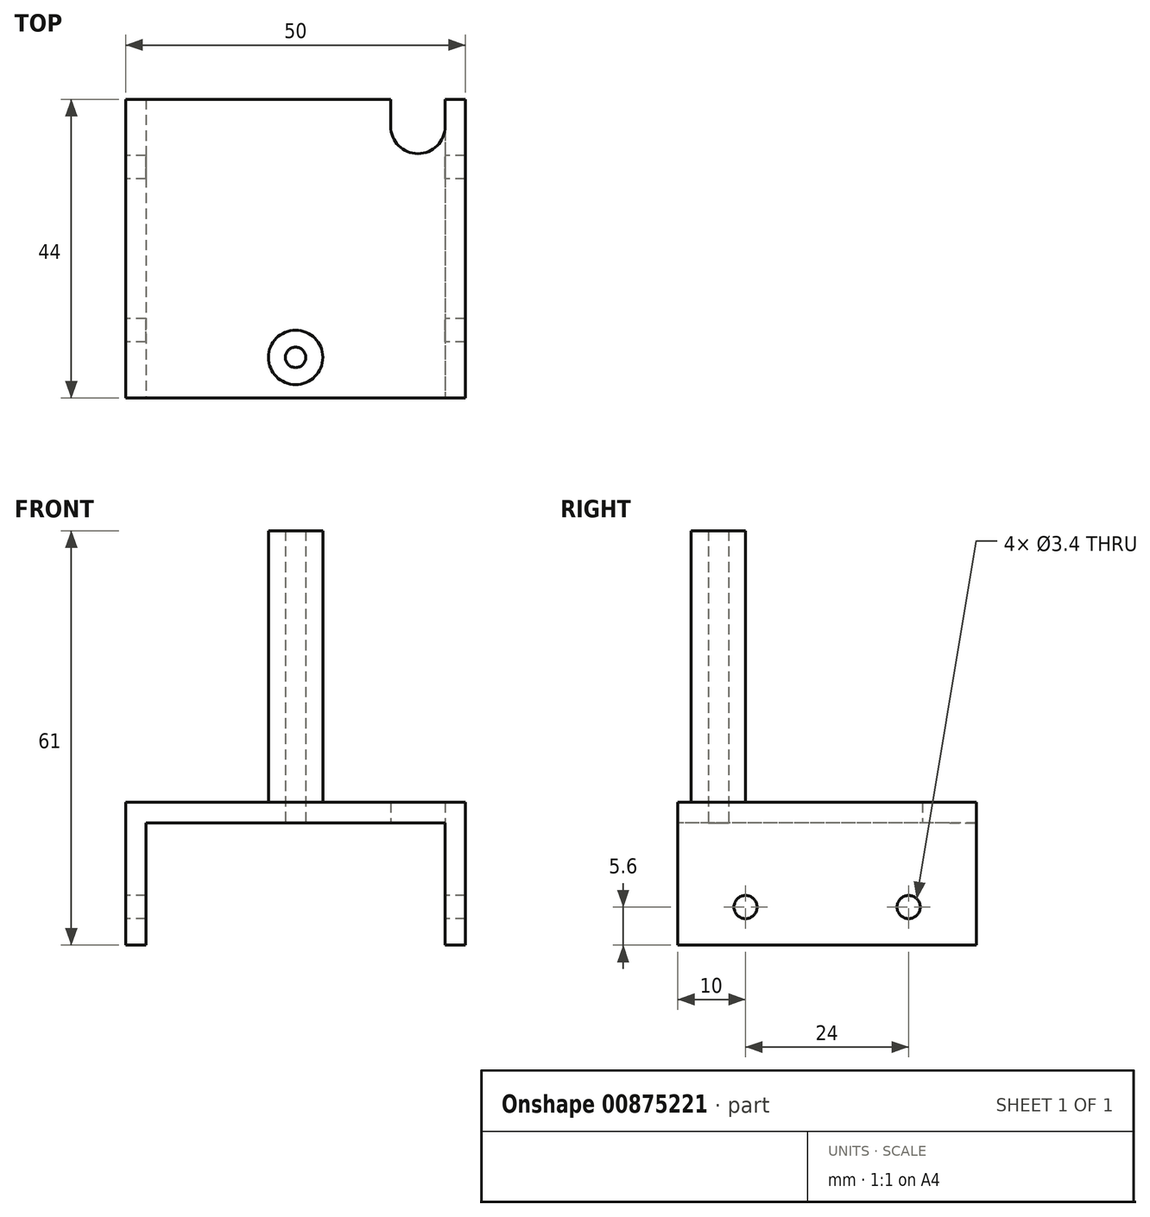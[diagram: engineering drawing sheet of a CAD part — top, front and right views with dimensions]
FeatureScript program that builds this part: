
annotation { "Feature Type Name" : "Feature", "Feature Type Description" : "" }
export const myFeature = defineFeature(function(context is Context, id is Id, definition is map)
    precondition{}
    {
        {
            var Q0;
            Q0=qCreatedBy(makeId("Top.planeOp"),FACE);
            var sketch = newSketch(context, id + "F0", { "sketchPlane" : qUnion([Q0])});
            skLineSegment(sketch, "E0.bottom", {"start": v(-22, 22) * mm, "end": v(22, 22) * mm});
            skLineSegment(sketch, "E0.top", {"start": v(-22, -22) * mm, "end": v(22, -22) * mm});
            skLineSegment(sketch, "E0.left", {"start": v(-22, 22) * mm, "end": v(-22, -22) * mm});
            skLineSegment(sketch, "E0.right", {"start": v(22, 22) * mm, "end": v(22, -22) * mm});
            skPoint(sketch, "E0.middle", {"position": v(0, 0) * mm});
            skCircle(sketch, "E1", {"center": v(18, 18) * mm, "radius": 4 * mm});
            skLineSegment(sketch, "E2", {"start": v(18, 18) * mm, "end": v(18, 22) * mm});
            skLineSegment(sketch, "E3", {"start": v(18, 18) * mm, "end": v(22, 18) * mm});
            skCircle(sketch, "E4", {"center": v(-17, -10) * mm, "radius": 1.7 * mm, "construction": true});
            skCircle(sketch, "E5", {"center": v(0, -16) * mm, "radius": 1.5 * mm});
            skCircle(sketch, "E6", {"center": v(3, -10) * mm, "radius": 1.7 * mm, "construction": true});
            skLineSegment(sketch, "E7", {"start": v(-22, -10) * mm, "end": v(22, -10) * mm, "construction": true});
            skLineSegment(sketch, "E8.bottom", {"start": v(-25, 22) * mm, "end": v(25, 22) * mm});
            skLineSegment(sketch, "E8.top", {"start": v(-25, -22) * mm, "end": v(25, -22) * mm});
            skLineSegment(sketch, "E8.left", {"start": v(-25, 22) * mm, "end": v(-25, -22) * mm});
            skLineSegment(sketch, "E8.right", {"start": v(25, 22) * mm, "end": v(25, -22) * mm});
            skCircle(sketch, "E9", {"center": v(0, -16) * mm, "radius": 4 * mm});
            skLineSegment(sketch, "E10", {"start": v(22, 18) * mm, "end": v(14, 18) * mm, "construction": true});
            skLineSegment(sketch, "E11", {"start": v(14, 18) * mm, "end": v(14, 22) * mm});
            skLineSegment(sketch, "E12.left", {"start": v(14, 22) * mm, "end": v(14, 18.38) * mm});
            skLineSegment(sketch, "E13.bottom", {"start": v(-22, 22) * mm, "end": v(22, 22) * mm, "construction": true});
            skLineSegment(sketch, "E14.top", {"start": v(-22, -14) * mm, "end": v(22, -14) * mm, "construction": true});
            skLineSegment(sketch, "E14.left", {"start": v(-22, -10) * mm, "end": v(-22, -14) * mm, "construction": true});
            skLineSegment(sketch, "E14.right", {"start": v(22, -10) * mm, "end": v(22, -14) * mm, "construction": true});
            skSolve(sketch);
        }
        {
            var Q0;
            {var subQ1=sQuery(id+"F0.wireOp",EDGE,"E0.top");Q0=makeQuery(id+"F0.imprint","IMPRINT",FACE,{"disambiguationData":[TD([[makeQuery(id+"F0.imprint","IMPRINT",EDGE,{"derivedFrom":subQ1}),1.0]])]});}
            var Q1;
            {var subQ0=sQuery(id+"F0.wireOp",EDGE,"E0.left");Q1=makeQuery(id+"F0.imprint","IMPRINT",FACE,{"disambiguationData":[TD([[makeQuery(id+"F0.imprint","IMPRINT",EDGE,{"derivedFrom":subQ0}),-1.0]])]});}
            var Q2;
            {var subQ1=sQuery(id+"F0.wireOp",EDGE,"E0.top");Q2=makeQuery(id+"F0.imprint","IMPRINT",FACE,{"disambiguationData":[TD([[makeQuery(id+"F0.imprint","IMPRINT",EDGE,{"derivedFrom":subQ1}),1.0]])]});}
            var Q3;
            {var subQ3=sQuery(id+"F0.wireOp",EDGE,"E8.right");Q3=makeQuery(id+"F0.imprint","IMPRINT",FACE,{"disambiguationData":[TD([[makeQuery(id+"F0.imprint","IMPRINT",EDGE,{"derivedFrom":subQ3}),-1.0]])]});}
            var Q4;
            Q4=makeQuery(id+"F0.imprint","IMPRINT",FACE,{"disambiguationData":[TD([[makeQuery(id+"F0.imprint","IMPRINT",EDGE,{"derivedFrom":sQuery(id+"F0.wireOp",EDGE,"E5")}),-1.0]])]});
            var Q5;
            Q5=makeQuery(id+"F0.imprint","IMPRINT",FACE,{"disambiguationData":[TD([[makeQuery(id+"F0.imprint","IMPRINT",EDGE,{"derivedFrom":sQuery(id+"F0.wireOp",EDGE,"rMzUnIo3-rhQd-p4DK-WS6P-ywbOph7gCmRt")}),1.0]])]});
            var Q6;
            Q6=makeQuery(id+"F0.imprint","IMPRINT",FACE,{"disambiguationData":[TD([[makeQuery(id+"F0.imprint","IMPRINT",EDGE,{"derivedFrom":sQuery(id+"F0.wireOp",EDGE,"x6sh83r0-H3hB-rSn6-KJVz-u5kGDsEZBk7Y.bottom")}),1.0]])]});
            var Q7;
            Q7=makeQuery(id+"F0.imprint","IMPRINT",FACE,{"disambiguationData":[TD([[makeQuery(id+"F0.imprint","IMPRINT",EDGE,{"derivedFrom":sQuery(id+"F0.wireOp",EDGE,"E4")}),-1.0]])]});
            var Q8;
            {var subQ3=sQuery(id+"F0.wireOp",EDGE,"wBAgPCPu-og1T-5jSz-0AmM-YHTr40DBTcPd.bottom");Q8=makeQuery(id+"F0.imprint","IMPRINT",FACE,{"disambiguationData":[TD([[makeQuery(id+"F0.imprint","IMPRINT",EDGE,{"derivedFrom":subQ3}),1.0]])]});}
            var Q9;
            {var subQ3=sQuery(id+"F0.wireOp",EDGE,"rCENyxZz-0AQo-YFxV-8mpq-i2NRhHaiGpbb.bottom");Q9=makeQuery(id+"F0.imprint","IMPRINT",FACE,{"disambiguationData":[TD([[makeQuery(id+"F0.imprint","IMPRINT",EDGE,{"derivedFrom":subQ3}),-1.0]])]});}
            var Q10;
            Q10=makeQuery(id+"F0.imprint","IMPRINT",FACE,{"disambiguationData":[TD([[makeQuery(id+"F0.imprint","IMPRINT",EDGE,{"derivedFrom":sQuery(id+"F0.wireOp",EDGE,"E12.bottom")}),1.0]])]});
            var Q11;
            Q11=makeQuery(id+"F0.imprint","IMPRINT",FACE,{"disambiguationData":[TD([[makeQuery(id+"F0.imprint","IMPRINT",EDGE,{"derivedFrom":sQuery(id+"F0.wireOp",EDGE,"E4")}),1.0]])]});
            var Q12;
            {var subQ0=sQuery(id+"F0.wireOp",EDGE,"rMzUnIo3-rhQd-p4DK-WS6P-ywbOph7gCmRt");var subQ1=sQuery(id+"F0.wireOp",EDGE,"E6");var subQ2=makeQuery(id+"F0.imprint","INTERSECT",VERTEX,{"disambiguationData":[OD(0.0)],"derivedFrom":[subQ1,subQ0]});Q12=makeQuery(id+"F0.imprint","IMPRINT",FACE,{"disambiguationData":[TD([[makeQuery(id+"F0.imprint","IMPRINT",EDGE,{"disambiguationData":[TD([[subQ2,1.0]])],"derivedFrom":subQ1}),1.0]])]});}
            var Q13;
            {var subQ0=sQuery(id+"F0.wireOp",EDGE,"rMzUnIo3-rhQd-p4DK-WS6P-ywbOph7gCmRt");var subQ1=sQuery(id+"F0.wireOp",EDGE,"E6");var subQ2=makeQuery(id+"F0.imprint","INTERSECT",VERTEX,{"disambiguationData":[OD(0.0)],"derivedFrom":[subQ1,subQ0]});Q13=makeQuery(id+"F0.imprint","IMPRINT",FACE,{"disambiguationData":[TD([[makeQuery(id+"F0.imprint","IMPRINT",EDGE,{"disambiguationData":[TD([[subQ2,-1.0]])],"derivedFrom":subQ1}),1.0]])]});}
            var Q14;
            Q14=makeQuery(id+"F0.imprint","IMPRINT",FACE,{"disambiguationData":[TD([[makeQuery(id+"F0.imprint","IMPRINT",EDGE,{"derivedFrom":sQuery(id+"F0.wireOp",EDGE,"8TfnTvCS-I4xh-Uub7-FGXd-pbQ1EKdAzu6P")}),1.0]])]});
            var Q15;
            Q15=makeQuery(id+"F0.imprint","IMPRINT",FACE,{"disambiguationData":[TD([[makeQuery(id+"F0.imprint","IMPRINT",EDGE,{"derivedFrom":sQuery(id+"F0.wireOp",EDGE,"KyL14QDJ-xpc4-ABvh-4uoX-4Ho8iOP7N066")}),1.0]])]});
            var Q16;
            Q16=makeQuery(id+"F0.imprint","IMPRINT",FACE,{"disambiguationData":[TD([[makeQuery(id+"F0.imprint","IMPRINT",EDGE,{"derivedFrom":sQuery(id+"F0.wireOp",EDGE,"ugW2MLtT-zH9N-anma-CMMo-lCa6m2wKbQ5z")}),1.0]])]});
            var Q17;
            Q17=makeQuery(id+"F0.imprint","IMPRINT",FACE,{"disambiguationData":[TD([[makeQuery(id+"F0.imprint","IMPRINT",EDGE,{"derivedFrom":sQuery(id+"F0.wireOp",EDGE,"uMU0c4zB-P3hA-kGCt-MizX-3QeWmNmszEBk")}),1.0]])]});
            extrude(context, id + "F1", {"entities" : qUnion([Q0, Q1, Q2, Q3, Q4, Q5, Q6, Q7, Q8, Q9, Q10, Q11, Q12, Q13, Q14, Q15, Q16, Q17]), "depth" : 3 * mm, "offsetDistance" : 25 * mm});
        }
        {
            var Q0;
            {var subQ0=sQuery(id+"F0.wireOp",EDGE,"E0.left");Q0=makeQuery(id+"F0.imprint","IMPRINT",FACE,{"disambiguationData":[TD([[makeQuery(id+"F0.imprint","IMPRINT",EDGE,{"derivedFrom":subQ0}),-1.0]])]});}
            var Q1;
            {var subQ3=sQuery(id+"F0.wireOp",EDGE,"E8.right");Q1=makeQuery(id+"F0.imprint","IMPRINT",FACE,{"disambiguationData":[TD([[makeQuery(id+"F0.imprint","IMPRINT",EDGE,{"derivedFrom":subQ3}),-1.0]])]});}
            extrude(context, id + "F2", {"entities" : qUnion([Q0, Q1]), "operationType" : NewBodyOperationType.ADD, "oppositeDirection" : true, "depth" : 18 * mm, "offsetDistance" : 25 * mm});
        }
        {
            var Q0;
            Q0=makeQuery(id+"F2.opExtrude","SWEPT_FACE",FACE,{"disambiguationData":[OSD([sQuery(id+"F0.wireOp",EDGE,"E0.left")])]});
            var sketch = newSketch(context, id + "F3", { "sketchPlane" : qUnion([Q0])});
            skLineSegment(sketch, "E15", {"start": v(-22, -12.4) * mm, "end": v(22, -12.4) * mm, "construction": true});
            skCircle(sketch, "E16", {"center": v(-12, -12.4) * mm, "radius": 1.7 * mm});
            skCircle(sketch, "E17", {"center": v(12, -12.4) * mm, "radius": 1.7 * mm});
            skSolve(sketch);
        }
        {
            var Q0;
            Q0=makeQuery(id+"F3.imprint","IMPRINT",FACE,{"disambiguationData":[TD([[makeQuery(id+"F3.imprint","IMPRINT",EDGE,{"derivedFrom":sQuery(id+"F3.wireOp",EDGE,"E16")}),1.0]])]});
            var Q1;
            Q1=makeQuery(id+"F3.imprint","IMPRINT",FACE,{"disambiguationData":[TD([[makeQuery(id+"F3.imprint","IMPRINT",EDGE,{"derivedFrom":sQuery(id+"F3.wireOp",EDGE,"E17")}),1.0]])]});
            var Q2;
            Q2=sQuery(id+"F3.wireOp",EDGE,"E16");
            var Q3;
            Q3=sQuery(id+"F3.wireOp",EDGE,"E17");
            extrude(context, id + "F4", {"entities" : qUnion([Q0, Q1]), "operationType" : NewBodyOperationType.REMOVE, "surfaceEntities" : qUnion([Q2, Q3]), "endBound" : BoundingType.SYMMETRIC, "depth" : 100 * mm, "offsetDistance" : 25 * mm});
        }
        {
            var Q0;
            Q0=makeQuery(id+"F0.imprint","IMPRINT",FACE,{"disambiguationData":[TD([[makeQuery(id+"F0.imprint","IMPRINT",EDGE,{"derivedFrom":sQuery(id+"F0.wireOp",EDGE,"E5")}),-1.0]])]});
            extrude(context, id + "F5", {"entities" : qUnion([Q0]), "operationType" : NewBodyOperationType.ADD, "depth" : 43 * mm, "offsetDistance" : 25 * mm});
        }
    });
